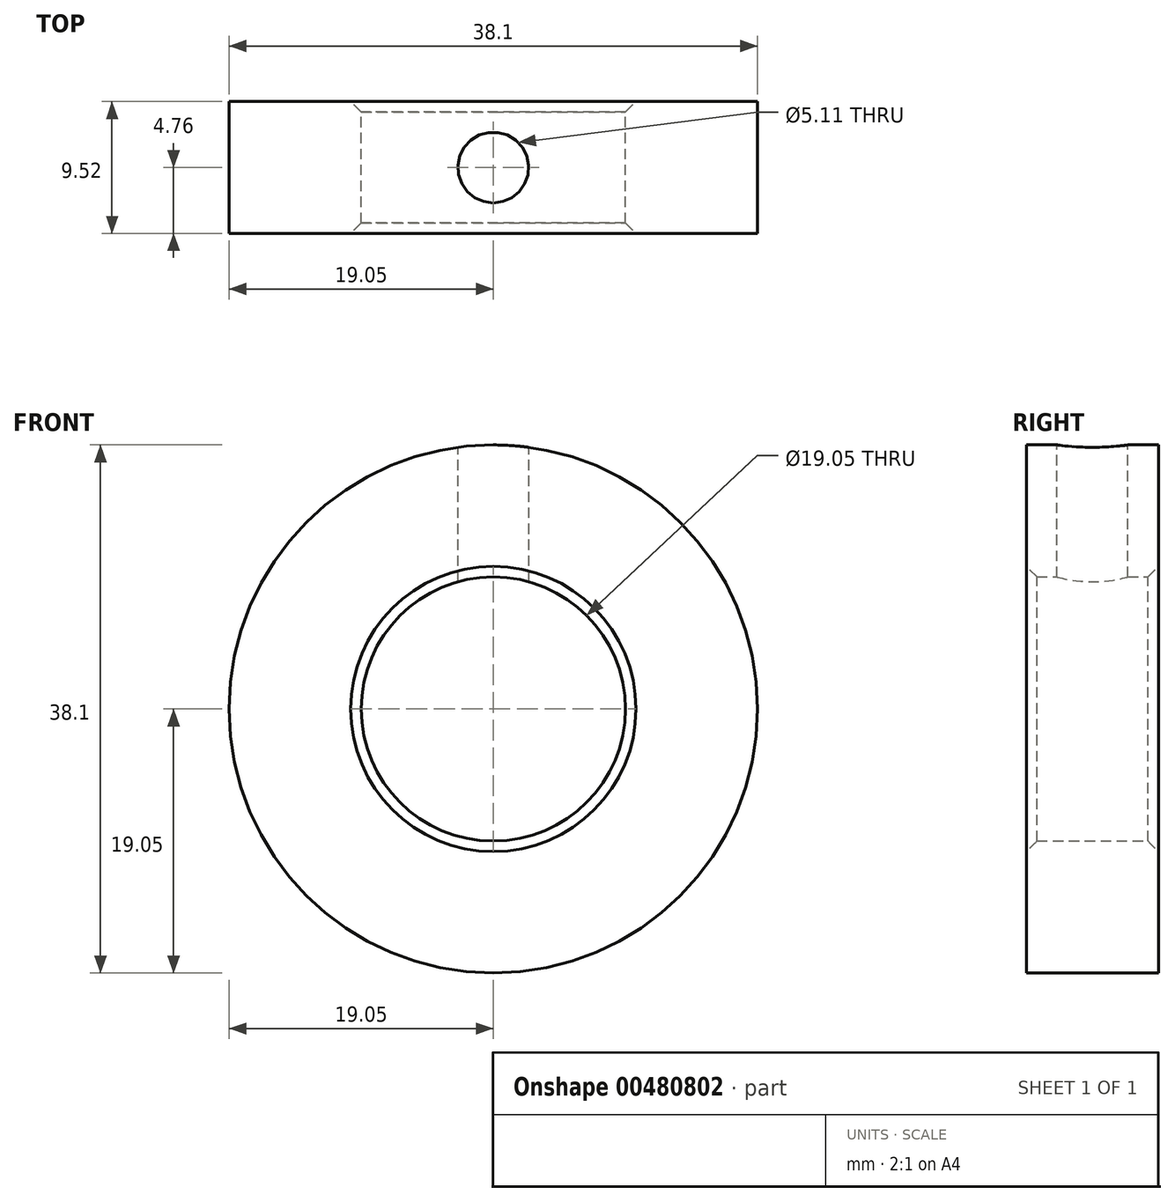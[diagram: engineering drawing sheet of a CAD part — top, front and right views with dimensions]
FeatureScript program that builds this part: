
annotation { "Feature Type Name" : "Feature", "Feature Type Description" : "" }
export const myFeature = defineFeature(function(context is Context, id is Id, definition is map)
    precondition{}
    {
        {
            var Q0;
            Q0=qCreatedBy(makeId("Front.planeOp"),FACE);
            var sketch = newSketch(context, id + "F0", { "sketchPlane" : qUnion([Q0])});
            skCircle(sketch, "E0", {"center": v(0, 0) * mm, "radius": 9.53 * mm});
            skCircle(sketch, "E1", {"center": v(0, 0) * mm, "radius": 19.05 * mm});
            skSolve(sketch);
        }
        {
            var Q0;
            Q0=makeQuery(id+"F0.imprint","IMPRINT",FACE,{"disambiguationData":[TD([[makeQuery(id+"F0.imprint","IMPRINT",EDGE,{"derivedFrom":sQuery(id+"F0.wireOp",EDGE,"E0")}),-1.0]])]});
            extrude(context, id + "F1", {"entities" : qUnion([Q0]), "endBound" : BoundingType.SYMMETRIC, "depth" : 9.52 * mm});
        }
        {
            var Q0;
            Q0=qCreatedBy(makeId("Top.planeOp"),FACE);
            cPlane(context, id + "F2", {"entities" : qUnion([Q0]), "cplaneType" : CPlaneType.OFFSET, "offset" : 19.05 * mm, "width" : 152.4 * mm, "height" : 152.4 * mm});
        }
        {
            var Q0;
            Q0=qCreatedBy(id+"F2.planeOp",FACE);
            var sketch = newSketch(context, id + "F3", { "sketchPlane" : qUnion([Q0])});
            skPoint(sketch, "E2", {"position": v(0, 0) * mm});
            skSolve(sketch);
        }
        {
            var Q0;
            Q0=sQuery(id+"F3.wireOp",VERTEX,"E2");
            var Q1;
            Q1=makeQuery(id+"F1.opExtrude","SWEPT_BODY",BODY,{"disambiguationData":[OSD([sQuery(id+"F0.wireOp",EDGE,"E0"),sQuery(id+"F0.wireOp",EDGE,"E1")])]});
            hole(context, id + "F4", {"style" : HoleStyle.SIMPLE, "endStyle" : HoleEndStyle.BLIND, "standardTappedOrClearance" : lookupTablePath({ "standard" : "ANSI", "engagement" : "75%", "pitch" : "20 tpi", "size" : "1/4", "type" : "Tapped" }), "standardBlindInLast" : lookupTablePath({ "standard" : "ANSI", "engagement" : "75%", "pitch" : "20 tpi", "size" : "1/4", "type" : "Tapped" }), "holeDiameter" : 5.1 * mm, "showTappedDepth" : true, "holeDepth" : 25.4 * mm, "tappedDepth" : 25.4 * mm, "tapClearance" : 0, "locations" : qUnion([Q0]), "scope" : qUnion([Q1]), "majorDiameter" : 6.35 * mm});
        }
        {
            var Q0;
            Q0=makeQuery(id+"F1.opExtrude","CAP_EDGE",EDGE,{"disambiguationData":[OSD([sQuery(id+"F0.wireOp",EDGE,"E0")])],"isStart":false});
            var Q1;
            Q1=makeQuery(id+"F1.opExtrude","CAP_EDGE",EDGE,{"disambiguationData":[OSD([sQuery(id+"F0.wireOp",EDGE,"E0")])],"isStart":true});
            chamfer(context, id + "F5", {"entities" : qUnion([Q0, Q1]), "width" : 0.76 * mm, "tangentPropagation" : true});
        }
    });
